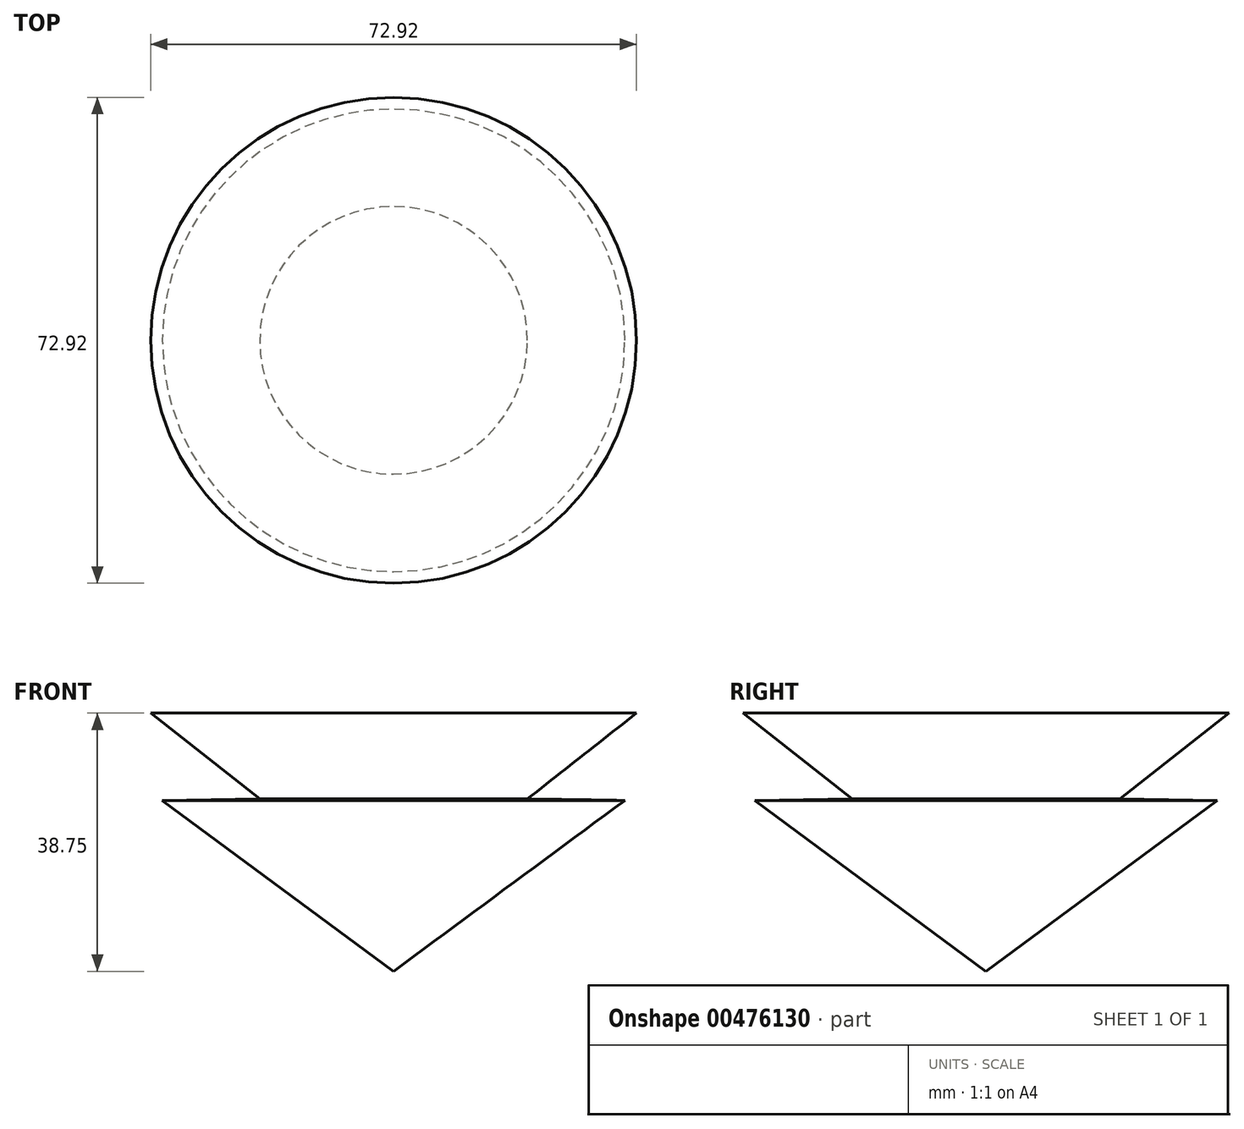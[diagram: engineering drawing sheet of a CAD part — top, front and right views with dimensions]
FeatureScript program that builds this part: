
annotation { "Feature Type Name" : "Feature", "Feature Type Description" : "" }
export const myFeature = defineFeature(function(context is Context, id is Id, definition is map)
    precondition{}
    {
        {
            var Q0;
            Q0=qCreatedBy(makeId("Front.planeOp"),FACE);
            var sketch = newSketch(context, id + "F0", { "sketchPlane" : qUnion([Q0])});
            skLineSegment(sketch, "E0", {"start": v(0, 0) * mm, "end": v(34.71, 25.65) * mm});
            skLineSegment(sketch, "E1", {"start": v(34.71, 25.65) * mm, "end": v(20.08, 25.87) * mm});
            skLineSegment(sketch, "E2", {"start": v(20.08, 25.87) * mm, "end": v(36.46, 38.75) * mm});
            skLineSegment(sketch, "E3", {"start": v(36.46, 38.75) * mm, "end": v(0, 38.75) * mm});
            skLineSegment(sketch, "E4", {"start": v(0, 38.75) * mm, "end": v(0, 0) * mm});
            skSolve(sketch);
        }
        {
            var Q0;
            Q0 = qSketchRegion(id + "F0", true);
            var Q1;
            Q1=makeQuery(id+"F0.imprint","IMPRINT",FACE,{"disambiguationData":[TD([[makeQuery(id+"F0.imprint","IMPRINT",EDGE,{"derivedFrom":sQuery(id+"F0.wireOp",EDGE,"E0")}),1.0]])]});
            var Q2;
            Q2=sQuery(id+"F0.wireOp",EDGE,"E4");
            revolve(context, id + "F1", {"entities" : qUnion([Q0, Q1]), "axis" : qUnion([Q2]), "revolveType" : RevolveType.FULL});
        }
    });
